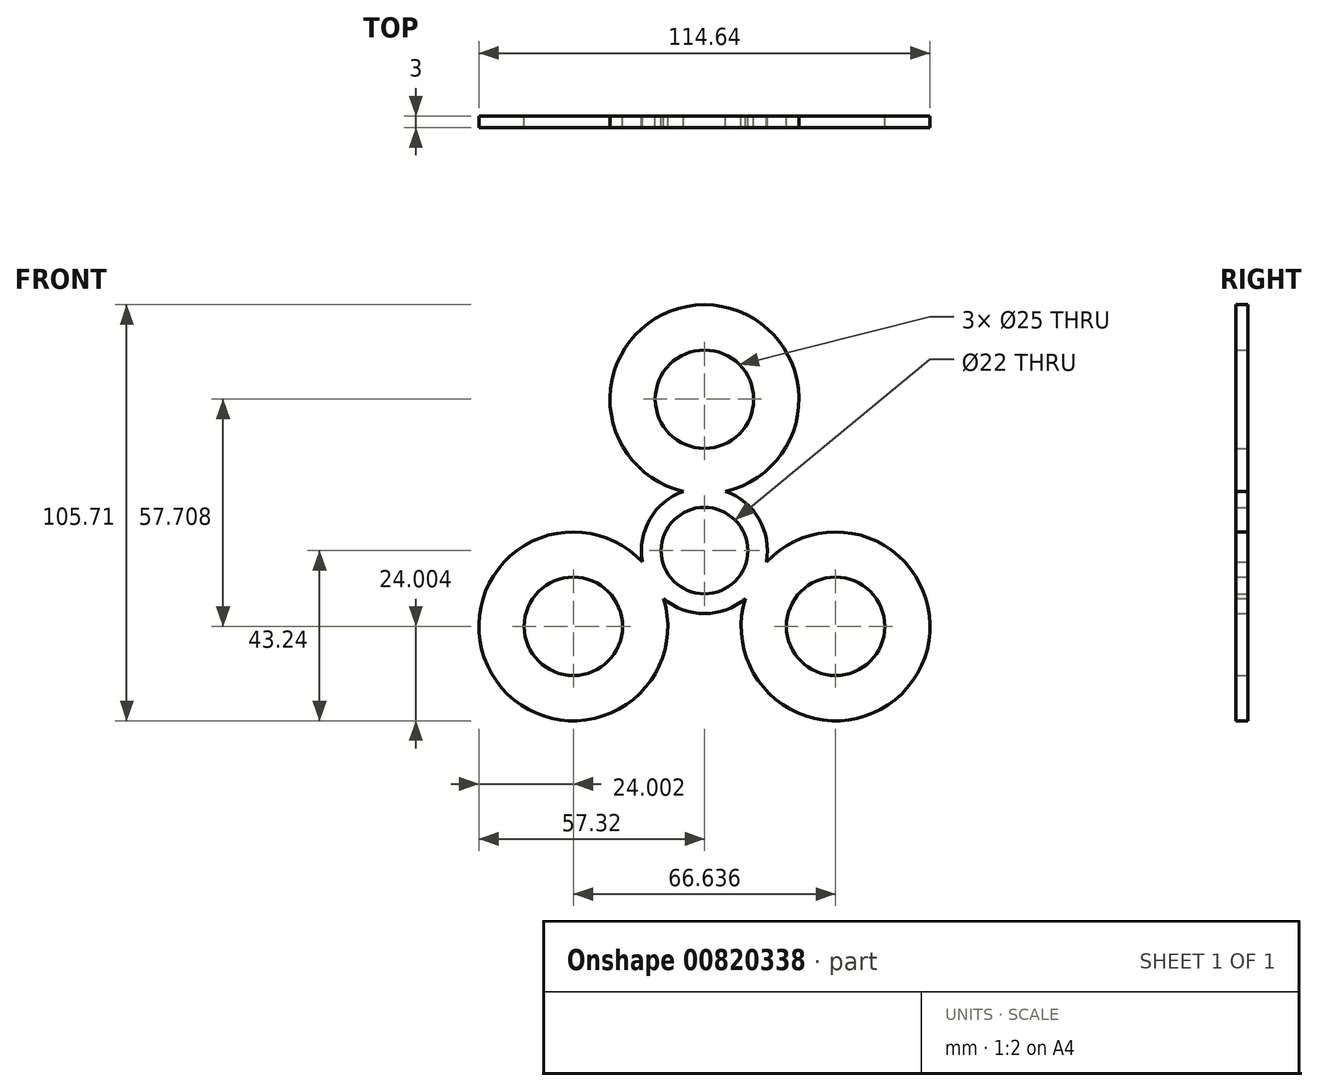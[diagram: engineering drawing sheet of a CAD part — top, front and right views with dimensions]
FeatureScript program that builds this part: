
annotation { "Feature Type Name" : "Feature", "Feature Type Description" : "" }
export const myFeature = defineFeature(function(context is Context, id is Id, definition is map)
    precondition{}
    {
        {
            var Q0;
            Q0=qCreatedBy(makeId("Front.planeOp"),FACE);
            var sketch = newSketch(context, id + "F0", { "sketchPlane" : qUnion([Q0])});
            skCircle(sketch, "E0", {"center": v(0, 0) * mm, "radius": 11 * mm});
            skArc(sketch, "E1", {"start": v(-5.36, 15.08) * mm, "mid": v(-13.86, 8) * mm, "end": v(-15.73, -2.9) * mm});
            skArc(sketch, "E2", {"start": v(5.36, 15.08) * mm, "mid": v(0, 62.47) * mm, "end": v(-5.36, 15.08) * mm});
            skCircle(sketch, "E3", {"center": v(0, 38.47) * mm, "radius": 12.5 * mm});
            skArc(sketch, "E4.1.0", {"start": v(-15.73, -2.9) * mm, "mid": v(-54.1, -31.24) * mm, "end": v(-10.38, -12.18) * mm});
            skCircle(sketch, "E4.1.1", {"center": v(-33.32, -19.24) * mm, "radius": 12.5 * mm});
            skArc(sketch, "E4.2.0", {"start": v(10.38, -12.18) * mm, "mid": v(54.1, -31.24) * mm, "end": v(15.73, -2.9) * mm});
            skCircle(sketch, "E4.2.1", {"center": v(33.32, -19.24) * mm, "radius": 12.5 * mm});
            skArc(sketch, "E5.trimOffspring", {"start": v(-10.38, -12.18) * mm, "mid": v(0, -16) * mm, "end": v(10.38, -12.18) * mm});
            skArc(sketch, "E6.trimOffspring", {"start": v(15.73, -2.9) * mm, "mid": v(13.86, 8) * mm, "end": v(5.36, 15.08) * mm});
            skSolve(sketch);
        }
        {
            var Q0;
            Q0=makeQuery(id+"F0.imprint","IMPRINT",FACE,{"disambiguationData":[TD([[makeQuery(id+"F0.imprint","IMPRINT",EDGE,{"derivedFrom":sQuery(id+"F0.wireOp",EDGE,"E0")}),-1.0]])]});
            extrude(context, id + "F1", {"entities" : qUnion([Q0]), "depth" : 3 * mm, "offsetDistance" : 25 * mm});
        }
    });
